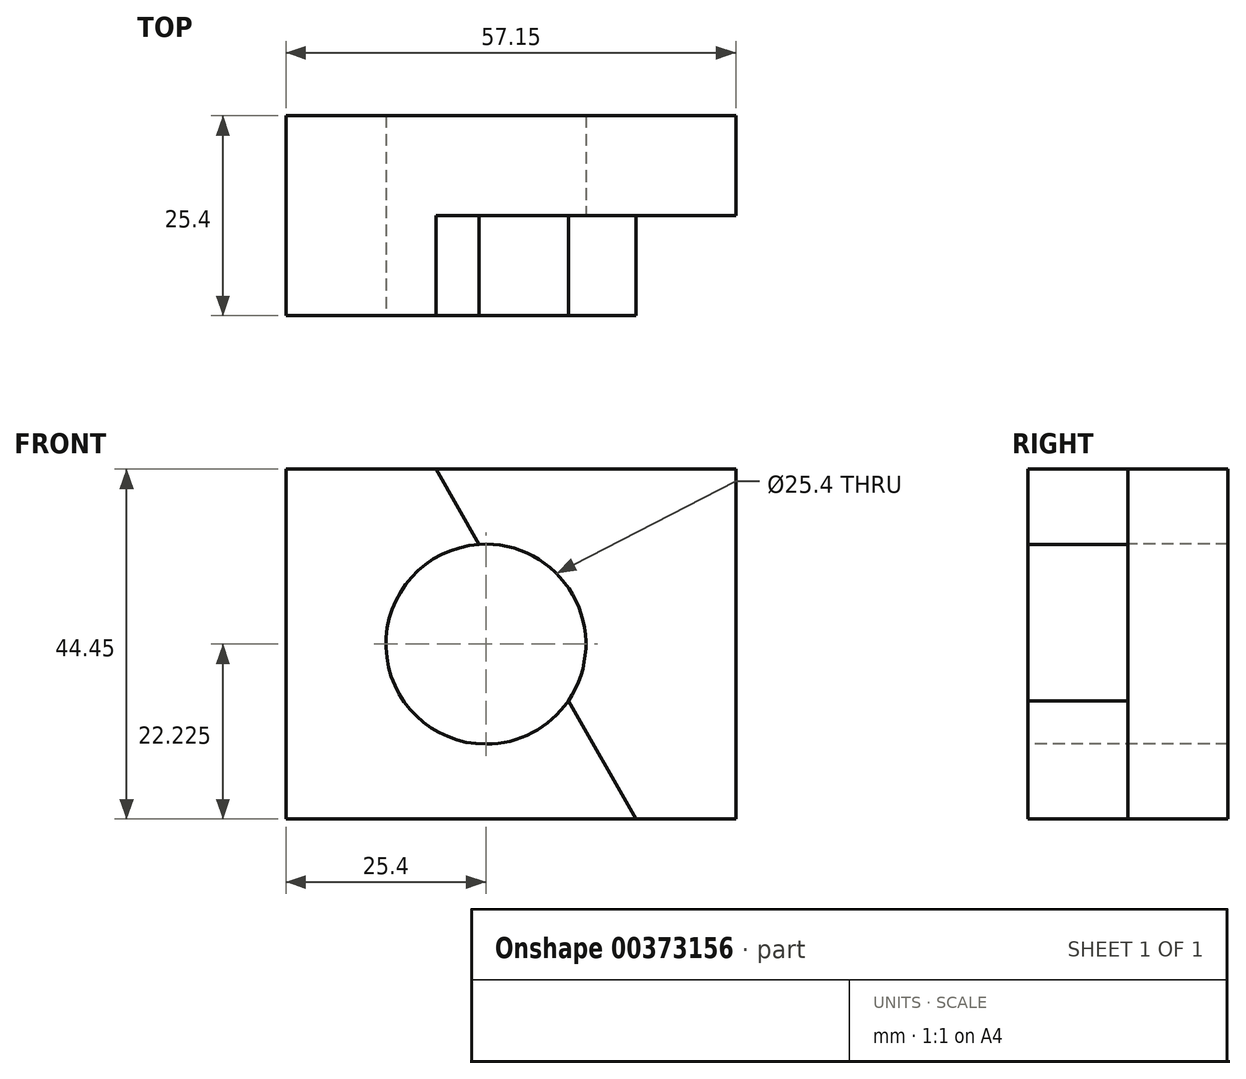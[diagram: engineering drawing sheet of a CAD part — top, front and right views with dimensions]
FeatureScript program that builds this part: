
annotation { "Feature Type Name" : "Feature", "Feature Type Description" : "" }
export const myFeature = defineFeature(function(context is Context, id is Id, definition is map)
    precondition{}
    {
        {
            var Q0;
            Q0=qCreatedBy(makeId("Front.planeOp"),FACE);
            var sketch = newSketch(context, id + "F0", { "sketchPlane" : qUnion([Q0])});
            skLineSegment(sketch, "E0", {"start": v(0, 0) * mm, "end": v(57.15, 0) * mm});
            skLineSegment(sketch, "E1", {"start": v(57.15, 0) * mm, "end": v(57.15, 44.45) * mm});
            skLineSegment(sketch, "E2", {"start": v(57.15, 44.45) * mm, "end": v(0, 44.45) * mm});
            skLineSegment(sketch, "E3", {"start": v(0, 44.45) * mm, "end": v(0, 0) * mm});
            skSolve(sketch);
        }
        {
            var Q0;
            Q0 = qSketchRegion(id + "F0", true);
            extrude(context, id + "F1", {"entities" : qUnion([Q0]), "oppositeDirection" : true, "depth" : 25.4 * mm});
        }
        {
            var Q0;
            Q0=makeQuery(id+"F1.opExtrude","CAP_FACE",FACE,{"disambiguationData":[OSD([sQuery(id+"F0.wireOp",EDGE,"E0"),sQuery(id+"F0.wireOp",EDGE,"E1"),sQuery(id+"F0.wireOp",EDGE,"E2"),sQuery(id+"F0.wireOp",EDGE,"E3")])],"isStart":true});
            var sketch = newSketch(context, id + "F2", { "sketchPlane" : qUnion([Q0])});
            skCircle(sketch, "E4", {"center": v(25.4, 22.23) * mm, "radius": 12.7 * mm});
            skPoint(sketch, "E5.start.orphan", {"position": v(0, 22.23) * mm});
            skSolve(sketch);
        }
        {
            var Q0;
            Q0 = qSketchRegion(id + "F2", true);
            extrude(context, id + "F3", {"entities" : qUnion([Q0]), "operationType" : NewBodyOperationType.REMOVE, "oppositeDirection" : true, "depth" : 25.4 * mm});
        }
        {
            var Q0;
            Q0=makeQuery(id+"F1.opExtrude","CAP_FACE",FACE,{"disambiguationData":[OSD([sQuery(id+"F0.wireOp",EDGE,"E0"),sQuery(id+"F0.wireOp",EDGE,"E1"),sQuery(id+"F0.wireOp",EDGE,"E2"),sQuery(id+"F0.wireOp",EDGE,"E3")])],"isStart":true});
            var sketch = newSketch(context, id + "F4", { "sketchPlane" : qUnion([Q0])});
            skLineSegment(sketch, "E6", {"start": v(57.15, 0) * mm, "end": v(57.15, 44.45) * mm});
            skLineSegment(sketch, "E7", {"start": v(57.15, 44.45) * mm, "end": v(19.05, 44.45) * mm});
            skLineSegment(sketch, "E8", {"start": v(19.05, 44.45) * mm, "end": v(44.45, 0) * mm});
            skLineSegment(sketch, "E9", {"start": v(44.45, 0) * mm, "end": v(57.15, 0) * mm});
            skSolve(sketch);
        }
        {
            var Q0;
            {var subQ0=sQuery(id+"F4.wireOp",EDGE,"E8");var subQ1=makeQuery(id+"F3.boolean.opBoolean","COPY",EDGE,{"derivedFrom":makeQuery(id+"F3.opExtrude","CAP_EDGE",EDGE,{"disambiguationData":[OSD([sQuery(id+"F2.wireOp",EDGE,"E4")])],"isStart":true})});var subQ2=makeQuery(id+"F4.imprint","INTERSECT",VERTEX,{"disambiguationData":[OD(0.0)],"derivedFrom":[subQ1,subQ0]});Q0=makeQuery(id+"F4.imprint","IMPRINT",FACE,{"disambiguationData":[TD([[makeQuery(id+"F4.imprint","IMPRINT",EDGE,{"disambiguationData":[TD([[subQ2,-1.0]])],"derivedFrom":subQ0}),1.0]])]});}
            var Q1;
            Q1=makeQuery(id+"F4.imprint","IMPRINT",FACE,{"disambiguationData":[TD([[makeQuery(id+"F4.imprint","IMPRINT",EDGE,{"derivedFrom":sQuery(id+"F4.wireOp",EDGE,"E6")}),1.0]])]});
            extrude(context, id + "F5", {"entities" : qUnion([Q0, Q1]), "operationType" : NewBodyOperationType.REMOVE, "oppositeDirection" : true, "depth" : 12.7 * mm});
        }
    });
